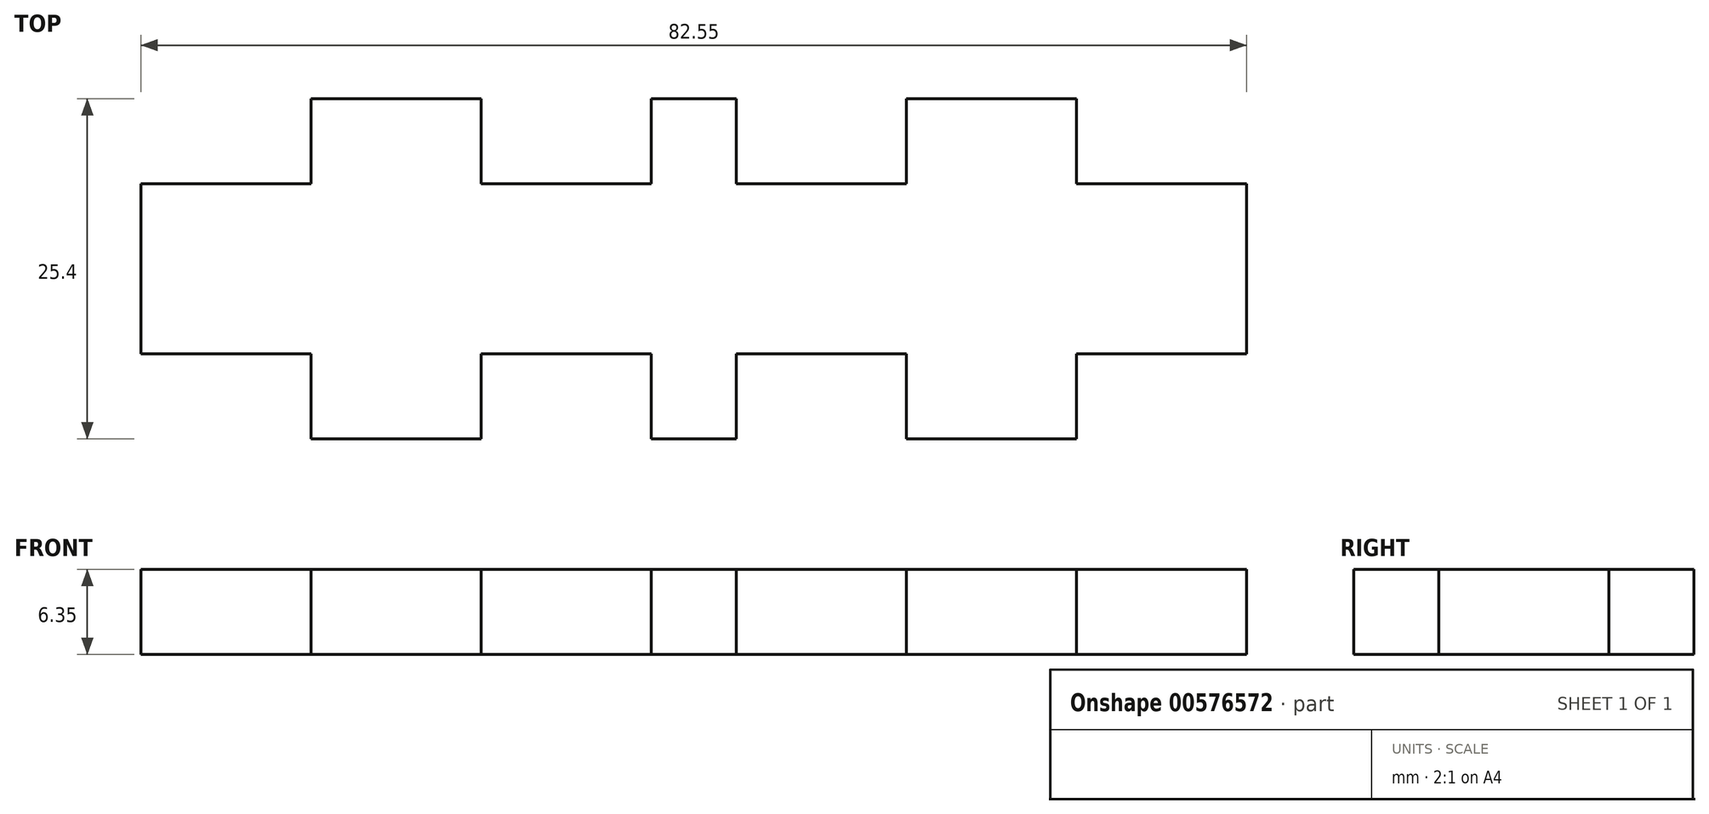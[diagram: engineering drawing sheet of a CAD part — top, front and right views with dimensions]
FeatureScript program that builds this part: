
annotation { "Feature Type Name" : "Feature", "Feature Type Description" : "" }
export const myFeature = defineFeature(function(context is Context, id is Id, definition is map)
    precondition{}
    {
        {
            var Q0;
            Q0=qCreatedBy(makeId("Top.planeOp"),FACE);
            var sketch = newSketch(context, id + "F0", { "sketchPlane" : qUnion([Q0])});
            skLineSegment(sketch, "E0.top", {"start": v(12.7, -25.4) * mm, "end": v(25.4, -25.4) * mm});
            skLineSegment(sketch, "E0.left", {"start": v(0, 0) * mm, "end": v(0, -19.05) * mm});
            skLineSegment(sketch, "E0.right", {"start": v(82.55, -6.35) * mm, "end": v(82.55, -19.05) * mm});
            skLineSegment(sketch, "E1", {"start": v(0, -6.35) * mm, "end": v(12.7, -6.35) * mm});
            skLineSegment(sketch, "E2", {"start": v(12.7, -6.35) * mm, "end": v(12.7, 0) * mm});
            skLineSegment(sketch, "E3", {"start": v(12.7, 0) * mm, "end": v(25.4, 0) * mm});
            skLineSegment(sketch, "E4", {"start": v(25.4, 0) * mm, "end": v(25.4, -6.35) * mm});
            skLineSegment(sketch, "E5", {"start": v(25.4, -6.35) * mm, "end": v(38.1, -6.35) * mm});
            skLineSegment(sketch, "E6", {"start": v(38.1, -6.35) * mm, "end": v(38.1, 0) * mm});
            skLineSegment(sketch, "E7", {"start": v(38.1, 0) * mm, "end": v(44.45, 0) * mm});
            skLineSegment(sketch, "E8", {"start": v(44.45, 0) * mm, "end": v(44.45, -6.35) * mm});
            skLineSegment(sketch, "E9", {"start": v(44.45, -6.35) * mm, "end": v(57.15, -6.35) * mm});
            skLineSegment(sketch, "E10", {"start": v(57.15, -6.35) * mm, "end": v(57.15, 0) * mm});
            skLineSegment(sketch, "E11", {"start": v(57.15, 0) * mm, "end": v(69.85, 0) * mm});
            skLineSegment(sketch, "E12", {"start": v(69.85, 0) * mm, "end": v(69.85, -6.35) * mm});
            skLineSegment(sketch, "E13", {"start": v(69.85, -6.35) * mm, "end": v(82.55, -6.35) * mm});
            skPoint(sketch, "E14.orphan", {"position": v(82.55, 0) * mm});
            skLineSegment(sketch, "E15", {"start": v(0, -6.35) * mm, "end": v(0, -19.05) * mm});
            skLineSegment(sketch, "E16", {"start": v(0, -19.05) * mm, "end": v(12.7, -19.05) * mm});
            skLineSegment(sketch, "E17", {"start": v(12.7, -19.05) * mm, "end": v(12.7, -25.4) * mm});
            skLineSegment(sketch, "E18", {"start": v(25.4, -25.4) * mm, "end": v(25.4, -19.05) * mm});
            skLineSegment(sketch, "E19", {"start": v(25.4, -19.05) * mm, "end": v(38.1, -19.05) * mm});
            skLineSegment(sketch, "E20", {"start": v(38.1, -19.05) * mm, "end": v(38.1, -25.4) * mm});
            skLineSegment(sketch, "E21", {"start": v(38.1, -25.4) * mm, "end": v(44.45, -25.4) * mm});
            skLineSegment(sketch, "E22", {"start": v(44.45, -25.4) * mm, "end": v(44.45, -19.05) * mm});
            skLineSegment(sketch, "E23", {"start": v(44.45, -19.05) * mm, "end": v(57.15, -19.05) * mm});
            skLineSegment(sketch, "E24", {"start": v(57.15, -19.05) * mm, "end": v(57.15, -25.4) * mm});
            skLineSegment(sketch, "E25", {"start": v(57.15, -25.4) * mm, "end": v(69.85, -25.4) * mm});
            skLineSegment(sketch, "E26", {"start": v(69.85, -25.4) * mm, "end": v(69.85, -19.05) * mm});
            skLineSegment(sketch, "E27", {"start": v(69.85, -19.05) * mm, "end": v(82.55, -19.05) * mm});
            skPoint(sketch, "E28.orphan", {"position": v(0, -25.4) * mm});
            skSolve(sketch);
        }
        {
            var Q0;
            Q0=makeQuery(id+"F0.imprint","IMPRINT",FACE,{"disambiguationData":[TD([[makeQuery(id+"F0.imprint","IMPRINT",EDGE,{"derivedFrom":sQuery(id+"F0.wireOp",EDGE,"E0.right")}),-1.0]])]});
            extrude(context, id + "F1", {"entities" : qUnion([Q0]), "depth" : 6.35 * mm, "offsetDistance" : 25.4 * mm});
        }
    });
